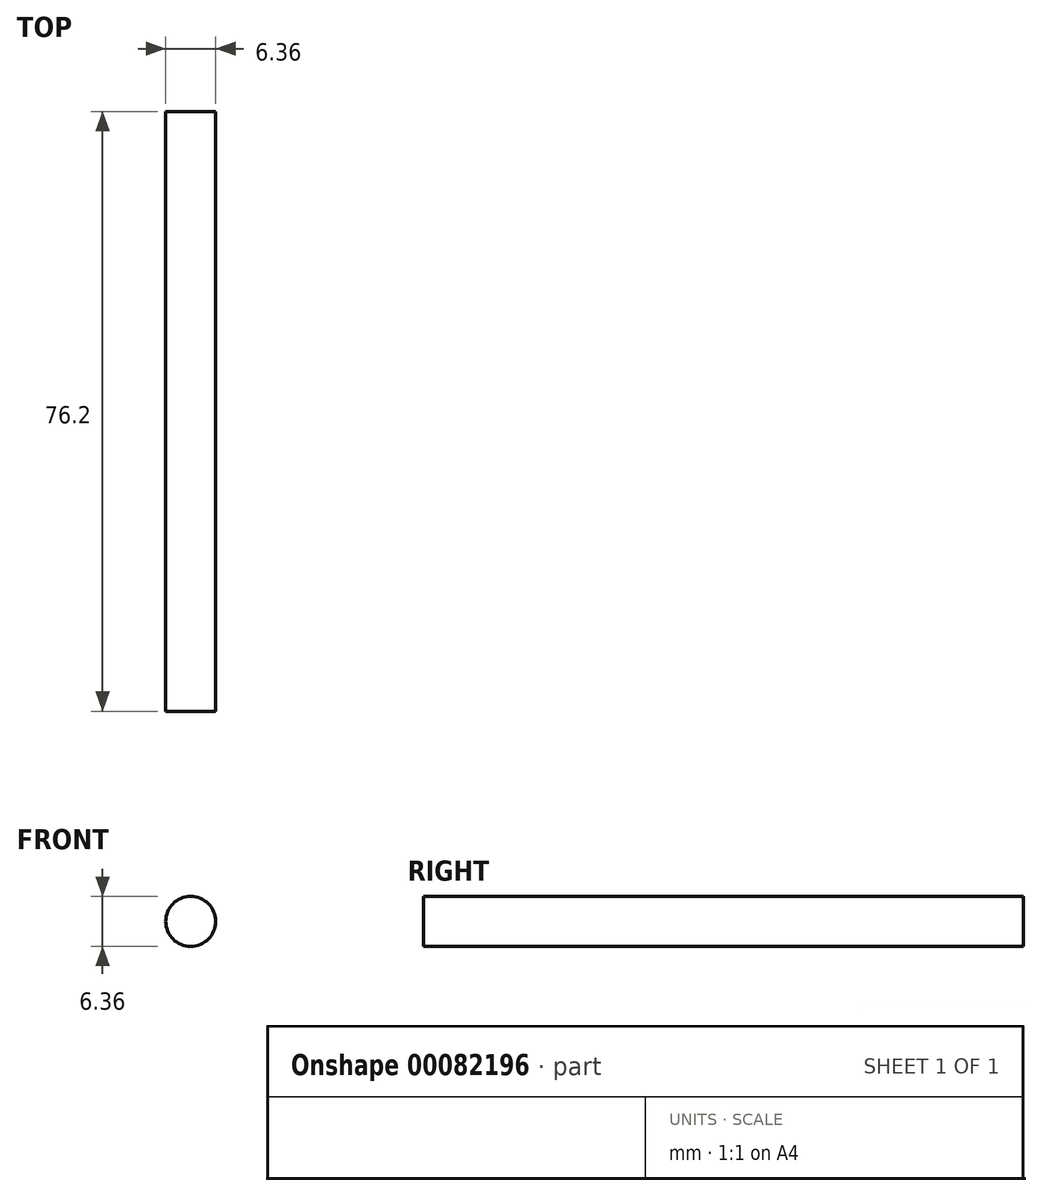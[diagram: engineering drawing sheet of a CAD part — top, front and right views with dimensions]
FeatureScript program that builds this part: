
annotation { "Feature Type Name" : "Feature", "Feature Type Description" : "" }
export const myFeature = defineFeature(function(context is Context, id is Id, definition is map)
    precondition{}
    {
        {
            var Q0;
            Q0=qCreatedBy(makeId("Front.planeOp"),FACE);
            var sketch = newSketch(context, id + "F0", { "sketchPlane" : qUnion([Q0])});
            skCircle(sketch, "E0", {"center": v(0, 0) * mm, "radius": 3.18 * mm});
            skSolve(sketch);
        }
        {
            var Q0;
            Q0 = qSketchRegion(id + "F0", true);
            extrude(context, id + "F1", {"entities" : qUnion([Q0]), "depth" : 76.2 * mm});
        }
    });
